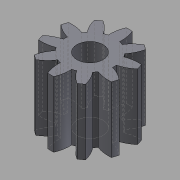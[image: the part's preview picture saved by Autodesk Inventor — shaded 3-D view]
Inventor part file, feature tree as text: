
AUTODESK INVENTOR PART (.ipt)
format: ipt  version: 2015 (Build 190159000, 159)  size: 182,784 bytes
history: native  units: mm (DEFAULTED — no unit token found)
features: plane x3, other x3, sketch x3, extrude x2
ambient origin geometry x8: Origin, YZ Plane, XZ Plane, XY Plane, X Axis, Y Axis, Z Axis, Center Point
bodies: Solid1 (feature_tree)
feature tree (11):
  extrude  "Extrusion1"  Depth=5.0mm TaperAngle=0.0deg
  plane  "Work Plane2"
  plane  "Work Plane8"
  plane  "Work Plane9"
  other  "Spur Gear"
  extrude  "Extrusion2"  Depth=10.0mm TaperAngle=0.0deg
  sketch  "Sketch1"  dims[d0=6.0mm d1=5.0mm d2=0.0mm]
  sketch  "Sketch2"  dims[d3=5.0mm d4=10.0mm d5=0.0mm]
  other  "Srf1"
  sketch  "Sketch3"  dims[d16=12.0mm d17=0.0mm d34=3.141593mm d39=0.0mm d41=0.0mm d43=12.0mm d46=12.0mm d47=0.0mm d48=0.0mm d49=2.0mm d50=10.0mm d51=0.0mm]
  other  "Pitch Diameter"
